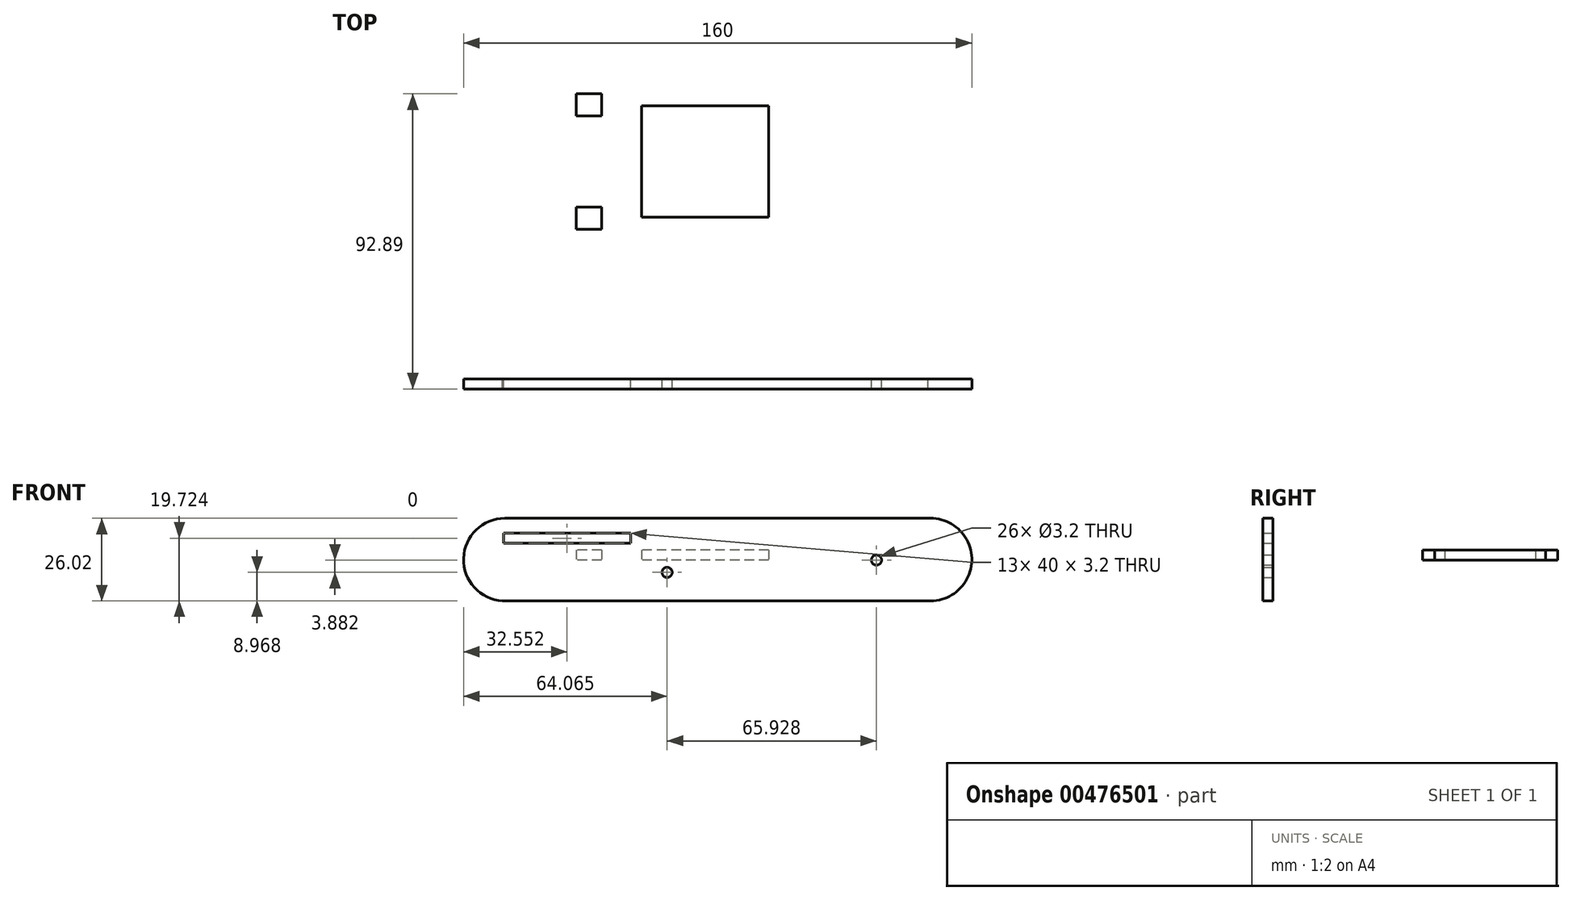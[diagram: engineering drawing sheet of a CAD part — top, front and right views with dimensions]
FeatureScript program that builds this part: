
annotation { "Feature Type Name" : "Feature", "Feature Type Description" : "" }
export const myFeature = defineFeature(function(context is Context, id is Id, definition is map)
    precondition{}
    {
        {
            var Q0;
            Q0=qCreatedBy(makeId("Front.planeOp"),FACE);
            var sketch = newSketch(context, id + "F0", { "sketchPlane" : qUnion([Q0])});
            skLineSegment(sketch, "E0", {"start": v(65.03, 13.17) * mm, "end": v(-68.95, 13.17) * mm});
            skLineSegment(sketch, "E1", {"start": v(-69.7, -12.83) * mm, "end": v(64.28, -12.83) * mm});
            skArc(sketch, "E2", {"start": v(65.03, 13.17) * mm, "mid": v(78.04, -0.21) * mm, "end": v(64.28, -12.83) * mm});
            skArc(sketch, "E3", {"start": v(-68.95, 13.17) * mm, "mid": v(-81.95, 0.54) * mm, "end": v(-69.7, -12.83) * mm});
            skCircle(sketch, "E4", {"center": v(48.03, 0) * mm, "radius": 1.6 * mm});
            skPoint(sketch, "E5", {"position": v(-69.4, 8.47) * mm});
            skPoint(sketch, "E6", {"position": v(-29.4, 5.27) * mm});
            skPoint(sketch, "E7", {"position": v(-50.92, 6.87) * mm});
            skLineSegment(sketch, "E8.bottom", {"start": v(-29.4, 5.27) * mm, "end": v(-69.4, 5.27) * mm});
            skLineSegment(sketch, "E8.top", {"start": v(-29.4, 8.47) * mm, "end": v(-69.4, 8.47) * mm});
            skLineSegment(sketch, "E8.left", {"start": v(-29.4, 5.27) * mm, "end": v(-29.4, 8.47) * mm});
            skLineSegment(sketch, "E8.right", {"start": v(-69.4, 5.27) * mm, "end": v(-69.4, 8.47) * mm});
            skCircle(sketch, "E9", {"center": v(-17.9, -3.88) * mm, "radius": 1.6 * mm});
            skSolve(sketch);
        }
        {
            var Q0;
            Q0=makeQuery(id+"F0.imprint","IMPRINT",FACE,{"disambiguationData":[TD([[makeQuery(id+"F0.imprint","IMPRINT",EDGE,{"derivedFrom":sQuery(id+"F0.wireOp",EDGE,"E0")}),1.0]])]});
            extrude(context, id + "F1", {"entities" : qUnion([Q0]), "depth" : 3.2 * mm, "offsetDistance" : 25 * mm});
        }
        {
            var Q0;
            Q0=qCreatedBy(makeId("Top.planeOp"),FACE);
            var sketch = newSketch(context, id + "F2", { "sketchPlane" : qUnion([Q0])});
            skLineSegment(sketch, "E10.bottom", {"start": v(14.09, 85.9) * mm, "end": v(-25.91, 85.9) * mm});
            skLineSegment(sketch, "E10.top", {"start": v(14.09, 50.9) * mm, "end": v(-25.91, 50.9) * mm});
            skLineSegment(sketch, "E10.left", {"start": v(14.09, 85.9) * mm, "end": v(14.09, 50.9) * mm});
            skLineSegment(sketch, "E10.right", {"start": v(-25.91, 85.9) * mm, "end": v(-25.91, 50.9) * mm});
            skLineSegment(sketch, "E11.bottom", {"start": v(-25.91, 82.7) * mm, "end": v(-46.52, 82.7) * mm});
            skLineSegment(sketch, "E11.top", {"start": v(-25.91, 54.1) * mm, "end": v(-46.52, 54.1) * mm});
            skLineSegment(sketch, "E11.left", {"start": v(-25.91, 82.7) * mm, "end": v(-25.91, 54.1) * mm, "construction": true});
            skLineSegment(sketch, "E11.right", {"start": v(-46.52, 82.7) * mm, "end": v(-46.52, 54.1) * mm});
            skPoint(sketch, "E12", {"position": v(13.48, 82.7) * mm});
            skLineSegment(sketch, "E13.bottom", {"start": v(13.48, 82.7) * mm, "end": v(-46.52, 82.7) * mm});
            skLineSegment(sketch, "E13.top", {"start": v(13.48, 54.1) * mm, "end": v(-46.52, 54.1) * mm});
            skLineSegment(sketch, "E13.left", {"start": v(13.48, 82.7) * mm, "end": v(13.48, 54.1) * mm});
            skCircle(sketch, "E14", {"center": v(-42, 68.4) * mm, "radius": 1.6 * mm});
            skLineSegment(sketch, "E15", {"start": v(-46.52, 82.7) * mm, "end": v(-46.52, 89.7) * mm});
            skLineSegment(sketch, "E16", {"start": v(-46.52, 89.7) * mm, "end": v(-38.52, 89.7) * mm});
            skLineSegment(sketch, "E17", {"start": v(-38.52, 89.7) * mm, "end": v(-38.52, 82.7) * mm});
            skLineSegment(sketch, "E18", {"start": v(-46.52, 47.1) * mm, "end": v(-38.52, 47.1) * mm});
            skLineSegment(sketch, "E19", {"start": v(-38.52, 47.1) * mm, "end": v(-38.52, 54.1) * mm});
            skLineSegment(sketch, "E20", {"start": v(-46.52, 47.1) * mm, "end": v(-46.52, 54.1) * mm});
            skSolve(sketch);
        }
        {
            var Q0;
            {var subQ1=sQuery(id+"F2.wireOp",EDGE,"E10.bottom");Q0=makeQuery(id+"F2.imprint","IMPRINT",FACE,{"disambiguationData":[TD([[makeQuery(id+"F2.imprint","IMPRINT",EDGE,{"derivedFrom":subQ1}),1.0]])]});}
            var Q1;
            {var subQ0=sQuery(id+"F2.wireOp",EDGE,"E13.bottom");var subQ1=sQuery(id+"F2.wireOp",EDGE,"E10.left");var subQ2=makeQuery(id+"F2.imprint","INTERSECT",VERTEX,{"derivedFrom":[subQ1,subQ0]});Q1=makeQuery(id+"F2.imprint","IMPRINT",FACE,{"disambiguationData":[TD([[makeQuery(id+"F2.imprint","IMPRINT",EDGE,{"disambiguationData":[TD([[subQ2,-1.0]])],"derivedFrom":subQ1}),-1.0]])]});}
            var Q2;
            {var subQ0=sQuery(id+"F2.wireOp",EDGE,"E10.top");Q2=makeQuery(id+"F2.imprint","IMPRINT",FACE,{"disambiguationData":[TD([[makeQuery(id+"F2.imprint","IMPRINT",EDGE,{"derivedFrom":subQ0}),-1.0]])]});}
            var Q3;
            {var subQ5=sQuery(id+"F2.wireOp",EDGE,"E11.right");Q3=makeQuery(id+"F2.imprint","IMPRINT",FACE,{"disambiguationData":[TD([[makeQuery(id+"F2.imprint","IMPRINT",EDGE,{"derivedFrom":subQ5}),1.0]])]});}
            var Q4;
            {var subQ5=sQuery(id+"F2.wireOp",EDGE,"E13.left");Q4=makeQuery(id+"F2.imprint","IMPRINT",FACE,{"disambiguationData":[TD([[makeQuery(id+"F2.imprint","IMPRINT",EDGE,{"derivedFrom":subQ5}),-1.0]])]});}
            var Q5;
            {var subQ0=sQuery(id+"F2.wireOp",EDGE,"E15");Q5=makeQuery(id+"F2.imprint","IMPRINT",FACE,{"disambiguationData":[TD([[makeQuery(id+"F2.imprint","IMPRINT",EDGE,{"derivedFrom":subQ0}),-1.0]])]});}
            var Q6;
            Q6=makeQuery(id+"F2.imprint","IMPRINT",FACE,{"disambiguationData":[TD([[makeQuery(id+"F2.imprint","IMPRINT",EDGE,{"derivedFrom":sQuery(id+"F2.wireOp",EDGE,"E18")}),1.0]])]});
            extrude(context, id + "F3", {"entities" : qUnion([Q0, Q1, Q2, Q3, Q4, Q5, Q6]), "depth" : 3.2 * mm, "offsetDistance" : 25 * mm});
        }
    });
